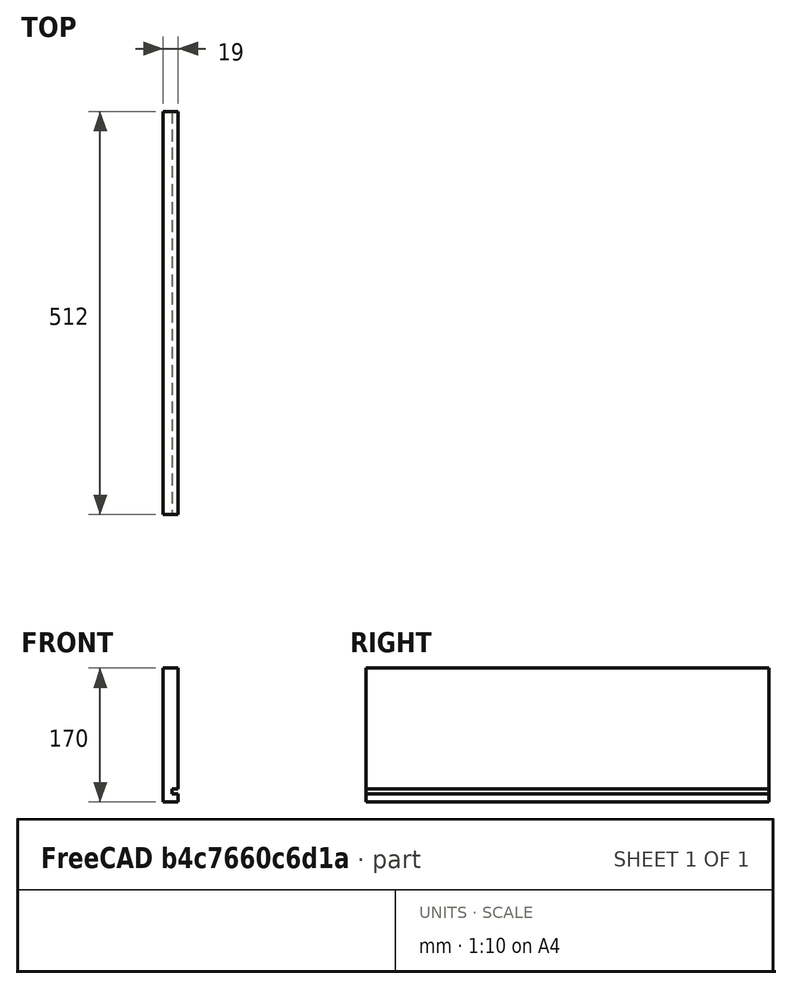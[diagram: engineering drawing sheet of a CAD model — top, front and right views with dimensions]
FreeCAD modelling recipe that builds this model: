
FCSTD DOCUMENT  (FreeCAD 1.0RUnknown)
Label: drawer_sides
License: All rights reserved
objects: PartDesign::CoordinateSystem×3, Sketcher::SketchObject×1, PartDesign::Pad×1, PartDesign::Body×1
note: 9 computed .brp shape members not serialized (recipe doc carries the construction recipe); baked Part::Feature solids carry a one-line shape summary decoded from their .brp
EXTERNAL_REF file=../../mastersketch.FCStd obj=Spreadsheet

FEATURE [Sketcher::SketchObject] Sketch
  ArcFitTolerance = 1e-06
  AttachmentSupport = -> [XZ_Plane]
  FullyConstrained = true
  MakeInternals = false
  MapMode = 5
  Placement = pos=(0,0,0) rot=(1,0,0;1.5708rad)
  expr: Constraints[13] = mastersketch#Spreadsheet.drawer_outer_thickness
  expr: Constraints[19] = mastersketch#Spreadsheet.drawer_bottom_thickness + mastersketch#Spreadsheet.drawer_bottom_tol
  expr: Constraints[20] = mastersketch#Spreadsheet.drawer_slot_height
  expr: Constraints[21] = mastersketch#Spreadsheet.drawer_height
  expr: Constraints[22] = mastersketch#Spreadsheet.drawer_slot_depth
  sketch-geometry (9):
    g0: LineSegment StartX=-9.5 StartY=-85 StartZ=0 EndX=9.5 EndY=-85 EndZ=0
    g1: LineSegment StartX=9.5 StartY=-85 StartZ=0 EndX=9.5 EndY=-75 EndZ=0
    g2: LineSegment StartX=9.5 StartY=85 StartZ=0 EndX=-9.5 EndY=85 EndZ=0
    g3: LineSegment StartX=-9.5 StartY=85 StartZ=0 EndX=-9.5 EndY=-85 EndZ=0
    g4: GeomPoint [constr] X=0 Y=0 Z=0
    g5: LineSegment StartX=9.5 StartY=-68.5 StartZ=0 EndX=1.5 EndY=-68.5 EndZ=0
    g6: LineSegment StartX=1.5 StartY=-68.5 StartZ=0 EndX=1.5 EndY=-75 EndZ=0
    g7: LineSegment StartX=1.5 StartY=-75 StartZ=0 EndX=9.5 EndY=-75 EndZ=0
    g8: LineSegment StartX=9.5 StartY=-68.5 StartZ=0 EndX=9.5 EndY=85 EndZ=0
  constraints (23):
    c: Coincident(g0,g1)
    c: Coincident(g8,g2)
    c: Coincident(g2,g3)
    c: Coincident(g3,g0)
    c: Horizontal(g0)
    c: Vertical(g1)
    c: Symmetric(g2,g0,g4)
    c: Coincident(g4,g-1)
    c: Coincident(g5,g6)
    c: Coincident(g6,g7)
    c: Vertical(g6)
    c: Horizontal(g5)
    c: Horizontal(g7)
    c: DistanceX(g2,g2) = 19
    c: Parallel(g3,g8)
    c: Coincident(g5,g8)
    c: Coincident(g7,g1)
    c: Vertical(g5,g1)
    c: Symmetric(g2,g2,g-2)
    c: Distance(g5,g1) = 6.5
    c: Distance(g6,g0) = 10
    c: DistanceY(g3,g3) = 170
    c: DistanceX(g5,g5) = 8
FEATURE [PartDesign::Pad] Pad
  Direction = (0,-1,2e-16)
  Length = 512
  Length2 = 10
  Placement = pos=(0,0,0) rot=(1,0,0;1.5708rad)
  Profile = -> Sketch
  ReferenceAxis = -> Sketch [N_Axis]
  Refine = true
  Suppressed = false
  Type = 0
  expr: Length = mastersketch#Spreadsheet.drawer_length - 2 * mastersketch#Spreadsheet.drawer_outer_thickness
FEATURE [PartDesign::CoordinateSystem] LCS_bottom_center
  AttacherType = Attacher::AttachEngine3D
  AttachmentSupport = -> [Pad]
  MapMode = 45
  Placement = pos=(-9.5,-256,-85) rot=(0,0.707107,0.707107;3.14159rad)
FEATURE [PartDesign::CoordinateSystem] LCS_1
  AttacherType = Attacher::AttachEngine3D
  AttachmentSupport = -> [Pad]
  MapMode = 7
  Placement = pos=(-9.5,-512,85) rot=(0,0,1;0rad)
FEATURE [PartDesign::CoordinateSystem] LCS_2
  AttacherType = Attacher::AttachEngine3D
  AttachmentSupport = -> [Pad]
  MapMode = 7
  Placement = pos=(-9.5,0,85) rot=(0,0,1;0rad)
FEATURE [PartDesign::Body] Body  label="drawer_sides"
  AllowCompound = false
  Group = -> [Sketch,Pad,LCS_bottom_center,LCS_1,LCS_2]
  Origin = -> Origin
  Tip = -> Pad
